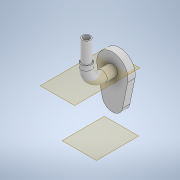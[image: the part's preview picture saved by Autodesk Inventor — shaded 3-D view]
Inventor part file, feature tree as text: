
AUTODESK INVENTOR PART (.ipt)
format: ipt  version: 2020 (Build 240168000, 168)  size: 176,128 bytes
history: native  units: in
note: dims shown in document units (in); Inventor stores cm internally (conversion verified against a paired STEP export)
features: sketch x4, extrude x3, plane x1, hole x1, other x1
ambient origin geometry x8: Origin, YZ Plane, XZ Plane, XY Plane, X Axis, Y Axis, Z Axis, Center Point
bodies: Body1 (feature_tree)
feature tree (10):
  extrude  "Extrusion8"  Depth=0.7874in
  extrude  "Extrusion9"  Depth=0.3937in
  plane  "Work Plane8"
  hole  "Hole1"  [1 undecoded]
  extrude  "Extrusion11"  Depth=0.7874in TaperAngle=0.0deg
  other  "Bend Part3"
  sketch  "Sketch8"  dims[d32=0.7874in d33=1.1811in]
  sketch  "Sketch13"  dims[d34=0.2756in d35=0.0in d36=0.3937in]
  sketch  "Sketch14"  dims[d37=1.9685in d38=0.0in]
  sketch  "Sketch15"  dims[d45=0.2362in d46=0.2362in d47=0.315in d48=0.2756in d49=90.0deg d50=0.315in d51=0.8108in d52=0.315in d53=0.7874in d54=0.0in d55=1.5748in d56=0.3937in d57=90.0deg d31=0.0197in]
note: 1 required parameter value undecoded (feature->parameter linkage not recoverable at this tier; creation-order binding heuristic only, values carry confidence <= 0.55)
